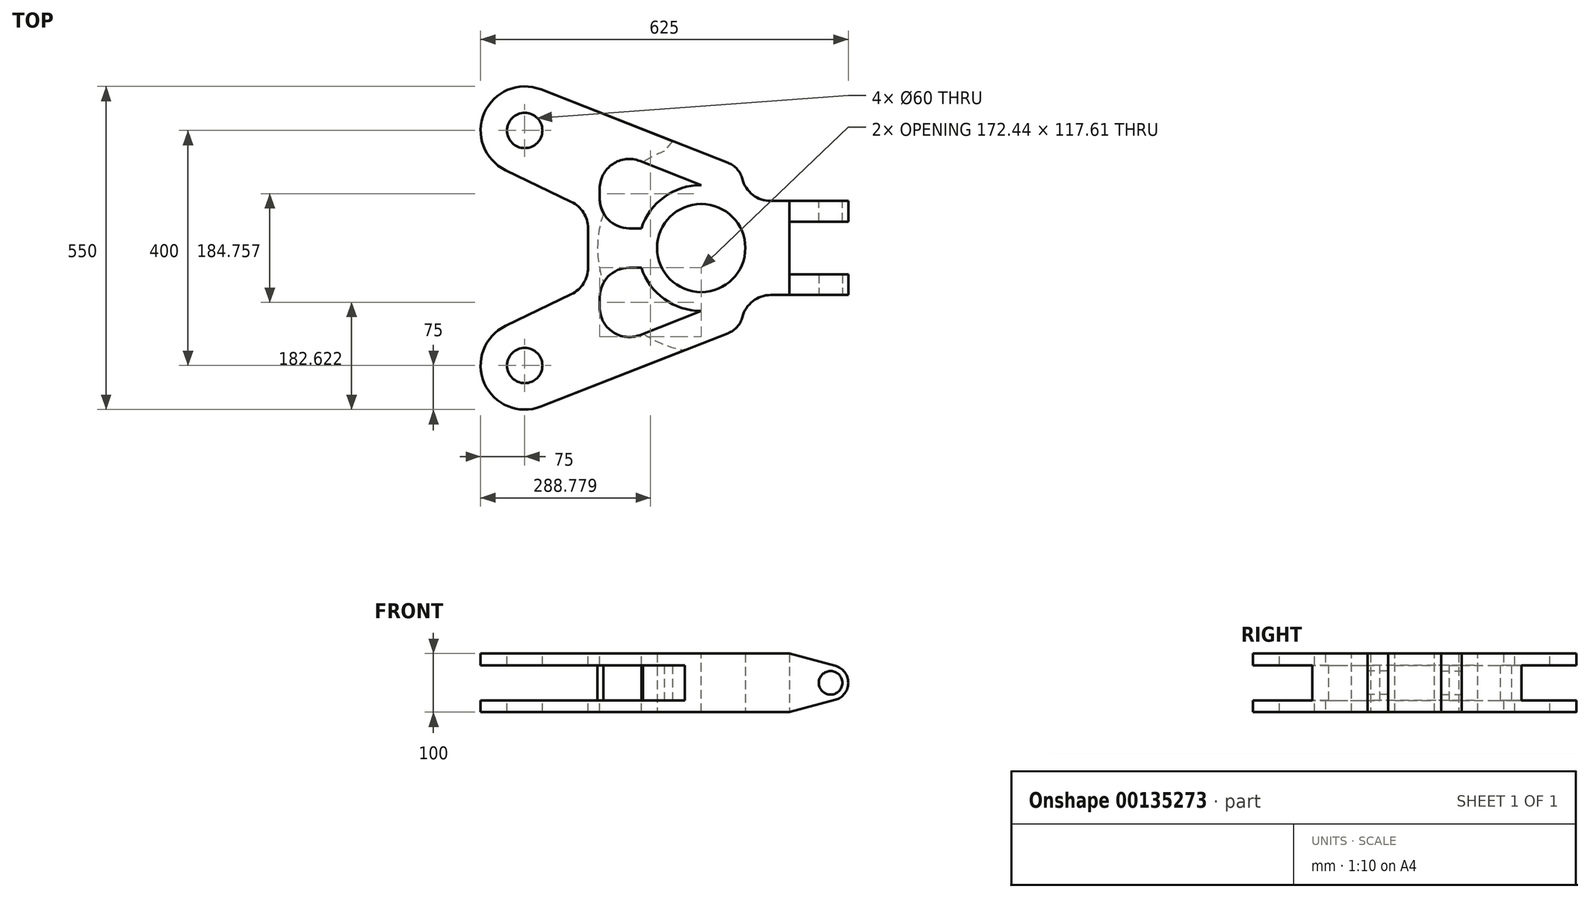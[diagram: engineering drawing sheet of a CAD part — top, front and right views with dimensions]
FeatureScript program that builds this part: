
annotation { "Feature Type Name" : "Feature", "Feature Type Description" : "" }
export const myFeature = defineFeature(function(context is Context, id is Id, definition is map)
    precondition{}
    {
        {
            var Q0;
            Q0=qCreatedBy(makeId("Top.planeOp"),FACE);
            var sketch = newSketch(context, id + "F0", { "sketchPlane" : qUnion([Q0])});
            skCircle(sketch, "E0", {"center": v(0, 0) * mm, "radius": 100 * mm});
            skCircle(sketch, "E1", {"center": v(0, 0) * mm, "radius": 75 * mm});
            skSolve(sketch);
        }
        {
            var Q0;
            Q0 = qSketchRegion(id + "F0", true);
            extrude(context, id + "F1", {"entities" : qUnion([Q0]), "endBound" : BoundingType.SYMMETRIC, "depth" : 100 * mm});
        }
        {
            var Q0;
            Q0=qCreatedBy(makeId("Right.planeOp"),FACE);
            cPlane(context, id + "F2", {"entities" : qUnion([Q0]), "cplaneType" : CPlaneType.OFFSET, "offset" : 150 * mm, "width" : 150 * mm, "height" : 150 * mm});
        }
        {
            var Q0;
            Q0=qCreatedBy(id+"F2.planeOp",FACE);
            var sketch = newSketch(context, id + "F3", { "sketchPlane" : qUnion([Q0])});
            skLineSegment(sketch, "E2.bottom", {"start": v(-80, 50) * mm, "end": v(80, 50) * mm});
            skLineSegment(sketch, "E2.top", {"start": v(-80, -50) * mm, "end": v(80, -50) * mm});
            skLineSegment(sketch, "E2.left", {"start": v(-80, 50) * mm, "end": v(-80, -50) * mm});
            skLineSegment(sketch, "E2.right", {"start": v(80, 50) * mm, "end": v(80, -50) * mm});
            skSolve(sketch);
        }
        {
            var Q0;
            Q0 = qSketchRegion(id + "F3", true);
            extrude(context, id + "F4", {"entities" : qUnion([Q0]), "operationType" : NewBodyOperationType.ADD, "endBound" : BoundingType.UP_TO_NEXT, "oppositeDirection" : true, "depth" : 25 * mm});
        }
        {
            var Q0;
            Q0=makeQuery(id+"F4.opExtrude","SWEPT_FACE",FACE,{"disambiguationData":[OSD([sQuery(id+"F3.wireOp",EDGE,"E2.left")])]});
            var sketch = newSketch(context, id + "F5", { "sketchPlane" : qUnion([Q0])});
            skArc(sketch, "E3", {"start": v(227.83, -28.96) * mm, "mid": v(250, 0) * mm, "end": v(227.83, 28.96) * mm});
            skLineSegment(sketch, "E4", {"start": v(150, 50) * mm, "end": v(227.83, 28.96) * mm});
            skLineSegment(sketch, "E5", {"start": v(150, -50) * mm, "end": v(227.83, -28.96) * mm});
            skLineSegment(sketch, "E6.0", {"start": v(150, 50) * mm, "end": v(150, -50) * mm});
            skSolve(sketch);
        }
        {
            var Q0;
            Q0=makeQuery(id+"F5.imprint","IMPRINT",FACE,{"disambiguationData":[TD([[makeQuery(id+"F5.imprint","IMPRINT",EDGE,{"derivedFrom":sQuery(id+"F5.wireOp",EDGE,"E3")}),1.0]])]});
            extrude(context, id + "F6", {"entities" : qUnion([Q0]), "operationType" : NewBodyOperationType.ADD, "oppositeDirection" : true, "depth" : 35 * mm});
        }
        {
            var Q0;
            Q0=sQuery(id+"F5.wireOp",VERTEX,"E3.center");
            var Q1;
            Q1=makeQuery(id+"F1.opExtrude","SWEPT_BODY",BODY,{"disambiguationData":[OSD([sQuery(id+"F0.wireOp",EDGE,"E0"),sQuery(id+"F0.wireOp",EDGE,"E1")])]});
            hole(context, id + "F7", {"style" : HoleStyle.SIMPLE, "endStyle" : HoleEndStyle.BLIND, "holeDiameter" : 40 * mm, "holeDepth" : 35 * mm, "locations" : qUnion([Q0]), "scope" : qUnion([Q1])});
        }
        {
            var Q0;
            Q0=makeQuery(id+"F4.opExtrude","SWEPT_FACE",FACE,{"disambiguationData":[OSD([sQuery(id+"F3.wireOp",EDGE,"E2.right")])]});
            var sketch = newSketch(context, id + "F8", { "sketchPlane" : qUnion([Q0])});
            skLineSegment(sketch, "E7.0", {"start": v(-150, 50) * mm, "end": v(-150, -50) * mm});
            skLineSegment(sketch, "E8.0", {"start": v(-150, 50) * mm, "end": v(-227.83, 28.96) * mm});
            skArc(sketch, "E9.0", {"start": v(-227.83, -28.96) * mm, "mid": v(-250, 0) * mm, "end": v(-227.83, 28.96) * mm});
            skLineSegment(sketch, "E10.0", {"start": v(-150, -50) * mm, "end": v(-227.83, -28.96) * mm});
            skSolve(sketch);
        }
        {
            var Q0;
            Q0=makeQuery(id+"F8.imprint","IMPRINT",FACE,{"disambiguationData":[TD([[makeQuery(id+"F8.imprint","IMPRINT",EDGE,{"derivedFrom":sQuery(id+"F8.wireOp",EDGE,"E7.0")}),-1.0]])]});
            extrude(context, id + "F9", {"entities" : qUnion([Q0]), "operationType" : NewBodyOperationType.ADD, "oppositeDirection" : true, "depth" : 35 * mm});
        }
        {
            var Q0;
            Q0=sQuery(id+"F8.wireOp",VERTEX,"E9.0.center");
            var Q1;
            Q1=makeQuery(id+"F1.opExtrude","SWEPT_BODY",BODY,{"disambiguationData":[OSD([sQuery(id+"F0.wireOp",EDGE,"E0"),sQuery(id+"F0.wireOp",EDGE,"E1")])]});
            hole(context, id + "F10", {"style" : HoleStyle.SIMPLE, "endStyle" : HoleEndStyle.BLIND, "holeDiameter" : 40 * mm, "holeDepth" : 35 * mm, "locations" : qUnion([Q0]), "scope" : qUnion([Q1])});
        }
        {
            var Q0;
            Q0=makeQuery(id+"F4.boolean.opBoolean","MERGE",FACE,{"derivedFrom":[makeQuery(id+"F1.opExtrude","CAP_FACE",FACE,{"disambiguationData":[OSD([sQuery(id+"F0.wireOp",EDGE,"E0"),sQuery(id+"F0.wireOp",EDGE,"E1")])],"isStart":false}),makeQuery(id+"F4.opExtrude","SWEPT_FACE",FACE,{"disambiguationData":[OSD([sQuery(id+"F3.wireOp",EDGE,"E2.bottom")])]})]});
            var sketch = newSketch(context, id + "F11", { "sketchPlane" : qUnion([Q0])});
            skArc(sketch, "E11", {"start": v(-332.53, -132.42) * mm, "mid": v(-368.75, -229.98) * mm, "end": v(-272.61, -269.82) * mm});
            skArc(sketch, "E12", {"start": v(-272.61, 269.82) * mm, "mid": v(-368.75, 229.98) * mm, "end": v(-332.53, 132.42) * mm});
            skLineSegment(sketch, "E13", {"start": v(-332.53, -132.42) * mm, "end": v(-192.44, -65) * mm});
            skLineSegment(sketch, "E14", {"start": v(-192.44, -65) * mm, "end": v(-192.44, 65) * mm});
            skLineSegment(sketch, "E15", {"start": v(-192.44, 65) * mm, "end": v(-332.53, 132.42) * mm});
            skArc(sketch, "E16", {"start": v(45.76, -144.95) * mm, "mid": v(70.22, -116.28) * mm, "end": v(60, -80) * mm});
            skArc(sketch, "E17", {"start": v(60, 80) * mm, "mid": v(70.22, 116.28) * mm, "end": v(45.76, 144.95) * mm});
            skArc(sketch, "E18.0", {"start": v(60, 80) * mm, "mid": v(-100, 0) * mm, "end": v(60, -80) * mm});
            skLineSegment(sketch, "E19", {"start": v(-272.61, -269.82) * mm, "end": v(45.76, -144.95) * mm});
            skLineSegment(sketch, "E20", {"start": v(-272.61, 269.82) * mm, "end": v(45.76, 144.95) * mm});
            skSolve(sketch);
        }
        {
            var Q0;
            Q0 = qSketchRegion(id + "F11", true);
            extrude(context, id + "F12", {"entities" : qUnion([Q0]), "operationType" : NewBodyOperationType.ADD, "oppositeDirection" : true, "depth" : 100 * mm});
        }
        {
            var Q0;
            {var subQ0=sQuery(id+"F3.wireOp",EDGE,"E2.left");Q0=makeQuery(id+"F12.boolean.opBoolean","MERGE",EDGE,{"derivedFrom":[makeQuery(id+"F4.opExtrude","TWEAK_EDGE",EDGE,{"derivedFrom":[makeQuery(id+"F1.opExtrude","SWEPT_FACE",FACE,{"disambiguationData":[OSD([sQuery(id+"F0.wireOp",EDGE,"E0")])]}),makeQuery(id+"F3.imprint","IMPRINT",EDGE,{"derivedFrom":subQ0})]}),makeQuery(id+"F12.opExtrude","SWEPT_EDGE",EDGE,{"disambiguationData":[OSD([sQuery(id+"F3.wireOp",EDGE,"E2.bottom"),subQ0,sQuery(id+"F11.wireOp",EDGE,"E16"),sQuery(id+"F11.wireOp",EDGE,"E18.0")])]})]});}
            var Q1;
            {var subQ0=sQuery(id+"F3.wireOp",EDGE,"E2.right");Q1=makeQuery(id+"F12.boolean.opBoolean","MERGE",EDGE,{"derivedFrom":[makeQuery(id+"F4.opExtrude","TWEAK_EDGE",EDGE,{"derivedFrom":[makeQuery(id+"F1.opExtrude","SWEPT_FACE",FACE,{"disambiguationData":[OSD([sQuery(id+"F0.wireOp",EDGE,"E0")])]}),makeQuery(id+"F3.imprint","IMPRINT",EDGE,{"derivedFrom":subQ0})]}),makeQuery(id+"F12.opExtrude","SWEPT_EDGE",EDGE,{"disambiguationData":[OSD([sQuery(id+"F3.wireOp",EDGE,"E2.bottom"),subQ0,sQuery(id+"F11.wireOp",EDGE,"E17"),sQuery(id+"F11.wireOp",EDGE,"E18.0")])]})]});}
            var Q2;
            Q2=makeQuery(id+"F12.opExtrude","SWEPT_EDGE",EDGE,{"disambiguationData":[OSD([sQuery(id+"F11.wireOp",EDGE,"E13"),sQuery(id+"F11.wireOp",EDGE,"E14")])]});
            var Q3;
            Q3=makeQuery(id+"F12.opExtrude","SWEPT_EDGE",EDGE,{"disambiguationData":[OSD([sQuery(id+"F11.wireOp",EDGE,"E14"),sQuery(id+"F11.wireOp",EDGE,"E15")])]});
            fillet(context, id + "F13", {"entities" : qUnion([Q0, Q1, Q2, Q3]), "radius" : 50 * mm, "tangentPropagation" : true, "allowEdgeOverflow" : false});
        }
        {
            var Q0;
            Q0=makeQuery(id+"F12.opExtrude","SWEPT_FACE",FACE,{"disambiguationData":[OSD([sQuery(id+"F11.wireOp",EDGE,"E19")])]});
            var sketch = newSketch(context, id + "F14", { "sketchPlane" : qUnion([Q0])});
            skLineSegment(sketch, "E21.bottom", {"start": v(-474.72, 30) * mm, "end": v(-89.73, 30) * mm});
            skLineSegment(sketch, "E21.top", {"start": v(-474.72, -30) * mm, "end": v(-89.73, -30) * mm});
            skLineSegment(sketch, "E21.left", {"start": v(-474.72, 30) * mm, "end": v(-474.72, -30) * mm});
            skLineSegment(sketch, "E21.right", {"start": v(-89.73, 30) * mm, "end": v(-89.73, -30) * mm});
            skSolve(sketch);
        }
        {
            var Q0;
            Q0=qCreatedBy(makeId("Front.planeOp"),FACE);
            var sketch = newSketch(context, id + "F15", { "sketchPlane" : qUnion([Q0])});
            skLineSegment(sketch, "E22", {"start": v(0, 73.43) * mm, "end": v(0, -184.04) * mm, "construction": true});
            skSolve(sketch);
        }
        {
            var Q0;
            Q0 = qSketchRegion(id + "F14", true);
            var Q1;
            Q1=sQuery(id+"F15.wireOp",EDGE,"E22");
            revolve(context, id + "F16", {"operationType" : NewBodyOperationType.REMOVE, "entities" : qUnion([Q0]), "axis" : qUnion([Q1]), "revolveType" : RevolveType.ONE_DIRECTION, "angle" : 150 * degree});
        }
        {
            var Q0;
            Q0=makeQuery(id+"F12.boolean.opBoolean","MERGE",FACE,{"derivedFrom":[makeQuery(id+"F4.boolean.opBoolean","MERGE",FACE,{"derivedFrom":[makeQuery(id+"F1.opExtrude","CAP_FACE",FACE,{"disambiguationData":[OSD([sQuery(id+"F0.wireOp",EDGE,"E0"),sQuery(id+"F0.wireOp",EDGE,"E1")])],"isStart":false}),makeQuery(id+"F4.opExtrude","SWEPT_FACE",FACE,{"disambiguationData":[OSD([sQuery(id+"F3.wireOp",EDGE,"E2.bottom")])]})]}),makeQuery(id+"F12.opExtrude","CAP_FACE",FACE,{"disambiguationData":[OSD([sQuery(id+"F11.wireOp",EDGE,"E11"),sQuery(id+"F11.wireOp",EDGE,"E12"),sQuery(id+"F11.wireOp",EDGE,"E13"),sQuery(id+"F11.wireOp",EDGE,"E14"),sQuery(id+"F11.wireOp",EDGE,"E15"),sQuery(id+"F11.wireOp",EDGE,"E16"),sQuery(id+"F11.wireOp",EDGE,"E17"),sQuery(id+"F11.wireOp",EDGE,"E18.0"),sQuery(id+"F11.wireOp",EDGE,"E19"),sQuery(id+"F11.wireOp",EDGE,"E20")])],"isStart":true})]});
            var sketch = newSketch(context, id + "F17", { "sketchPlane" : qUnion([Q0])});
            skPoint(sketch, "E23", {"position": v(-300, 200) * mm});
            skPoint(sketch, "E24", {"position": v(-300, -200) * mm});
            skSolve(sketch);
        }
        {
            var Q0;
            Q0=sQuery(id+"F17.wireOp",VERTEX,"E23");
            var Q1;
            Q1=sQuery(id+"F17.wireOp",VERTEX,"E24");
            var Q2;
            Q2=makeQuery(id+"F1.opExtrude","SWEPT_BODY",BODY,{"disambiguationData":[OSD([sQuery(id+"F0.wireOp",EDGE,"E0"),sQuery(id+"F0.wireOp",EDGE,"E1")])]});
            hole(context, id + "F18", {"style" : HoleStyle.SIMPLE, "endStyle" : HoleEndStyle.BLIND, "holeDiameter" : 60 * mm, "holeDepth" : 100 * mm, "locations" : qUnion([Q0, Q1]), "scope" : qUnion([Q2])});
        }
        {
            var Q0;
            Q0=makeQuery(id+"F12.boolean.opBoolean","MERGE",FACE,{"derivedFrom":[makeQuery(id+"F4.boolean.opBoolean","MERGE",FACE,{"derivedFrom":[makeQuery(id+"F1.opExtrude","CAP_FACE",FACE,{"disambiguationData":[OSD([sQuery(id+"F0.wireOp",EDGE,"E0"),sQuery(id+"F0.wireOp",EDGE,"E1")])],"isStart":false}),makeQuery(id+"F4.opExtrude","SWEPT_FACE",FACE,{"disambiguationData":[OSD([sQuery(id+"F3.wireOp",EDGE,"E2.bottom")])]})]}),makeQuery(id+"F12.opExtrude","CAP_FACE",FACE,{"disambiguationData":[OSD([sQuery(id+"F11.wireOp",EDGE,"E11"),sQuery(id+"F11.wireOp",EDGE,"E12"),sQuery(id+"F11.wireOp",EDGE,"E13"),sQuery(id+"F11.wireOp",EDGE,"E14"),sQuery(id+"F11.wireOp",EDGE,"E15"),sQuery(id+"F11.wireOp",EDGE,"E16"),sQuery(id+"F11.wireOp",EDGE,"E17"),sQuery(id+"F11.wireOp",EDGE,"E18.0"),sQuery(id+"F11.wireOp",EDGE,"E19"),sQuery(id+"F11.wireOp",EDGE,"E20")])],"isStart":true})]});
            var sketch = newSketch(context, id + "F19", { "sketchPlane" : qUnion([Q0])});
            skArc(sketch, "E25", {"start": v(-101.78, -33.57) * mm, "mid": v(-62.8, -86.85) * mm, "end": v(0, -107.18) * mm});
            skLineSegment(sketch, "E26", {"start": v(-172.44, -33.57) * mm, "end": v(-101.78, -33.57) * mm});
            skLineSegment(sketch, "E27", {"start": v(-172.44, -174.82) * mm, "end": v(0, -107.18) * mm});
            skPoint(sketch, "E28.0.end.orphan", {"position": v(-192.44, 33.57) * mm});
            skPoint(sketch, "E28.0.start.orphan", {"position": v(-192.44, -33.57) * mm});
            skLineSegment(sketch, "E29", {"start": v(-172.44, -33.57) * mm, "end": v(-172.44, -174.82) * mm});
            skLineSegment(sketch, "E30.MirrorCS", {"start": v(-172.44, 174.82) * mm, "end": v(0, 107.18) * mm});
            skArc(sketch, "E31.MirrorCS", {"start": v(-101.78, 33.57) * mm, "mid": v(-62.8, 86.85) * mm, "end": v(0, 107.18) * mm});
            skLineSegment(sketch, "E32.MirrorCS", {"start": v(-172.44, 33.57) * mm, "end": v(-172.44, 174.82) * mm});
            skLineSegment(sketch, "E33.MirrorCS", {"start": v(-172.44, 33.57) * mm, "end": v(-101.78, 33.57) * mm});
            skSolve(sketch);
        }
        {
            var Q0;
            Q0 = qSketchRegion(id + "F19", true);
            extrude(context, id + "F20", {"entities" : qUnion([Q0]), "operationType" : NewBodyOperationType.REMOVE, "oppositeDirection" : true, "depth" : 100 * mm});
        }
        {
            var Q0;
            Q0=makeQuery(id+"F20.boolean.opBoolean","COPY",EDGE,{"derivedFrom":makeQuery(id+"F20.opExtrude","SWEPT_EDGE",EDGE,{"disambiguationData":[OSD([sQuery(id+"F19.wireOp",EDGE,"E26"),sQuery(id+"F19.wireOp",EDGE,"E29")])]})});
            var Q1;
            Q1=makeQuery(id+"F20.boolean.opBoolean","COPY",EDGE,{"disambiguationData":[OD(0.0)],"derivedFrom":makeQuery(id+"F20.opExtrude","SWEPT_EDGE",EDGE,{"disambiguationData":[OSD([sQuery(id+"F19.wireOp",EDGE,"E27"),sQuery(id+"F19.wireOp",EDGE,"E29")])]})});
            var Q2;
            Q2=makeQuery(id+"F20.boolean.opBoolean","COPY",EDGE,{"disambiguationData":[OD(1.0)],"derivedFrom":makeQuery(id+"F20.opExtrude","SWEPT_EDGE",EDGE,{"disambiguationData":[OSD([sQuery(id+"F19.wireOp",EDGE,"E27"),sQuery(id+"F19.wireOp",EDGE,"E29")])]})});
            var Q3;
            Q3=makeQuery(id+"F20.boolean.opBoolean","COPY",EDGE,{"derivedFrom":makeQuery(id+"F20.opExtrude","SWEPT_EDGE",EDGE,{"disambiguationData":[OSD([sQuery(id+"F19.wireOp",EDGE,"E32.MirrorCS"),sQuery(id+"F19.wireOp",EDGE,"E33.MirrorCS")])]})});
            var Q4;
            Q4=makeQuery(id+"F20.boolean.opBoolean","COPY",EDGE,{"disambiguationData":[OD(1.0)],"derivedFrom":makeQuery(id+"F20.opExtrude","SWEPT_EDGE",EDGE,{"disambiguationData":[OSD([sQuery(id+"F19.wireOp",EDGE,"E30.MirrorCS"),sQuery(id+"F19.wireOp",EDGE,"E32.MirrorCS")])]})});
            var Q5;
            Q5=makeQuery(id+"F20.boolean.opBoolean","COPY",EDGE,{"disambiguationData":[OD(0.0)],"derivedFrom":makeQuery(id+"F20.opExtrude","SWEPT_EDGE",EDGE,{"disambiguationData":[OSD([sQuery(id+"F19.wireOp",EDGE,"E30.MirrorCS"),sQuery(id+"F19.wireOp",EDGE,"E32.MirrorCS")])]})});
            fillet(context, id + "F21", {"entities" : qUnion([Q0, Q1, Q2, Q3, Q4, Q5]), "radius" : 50 * mm, "tangentPropagation" : true, "allowEdgeOverflow" : false});
        }
    });
